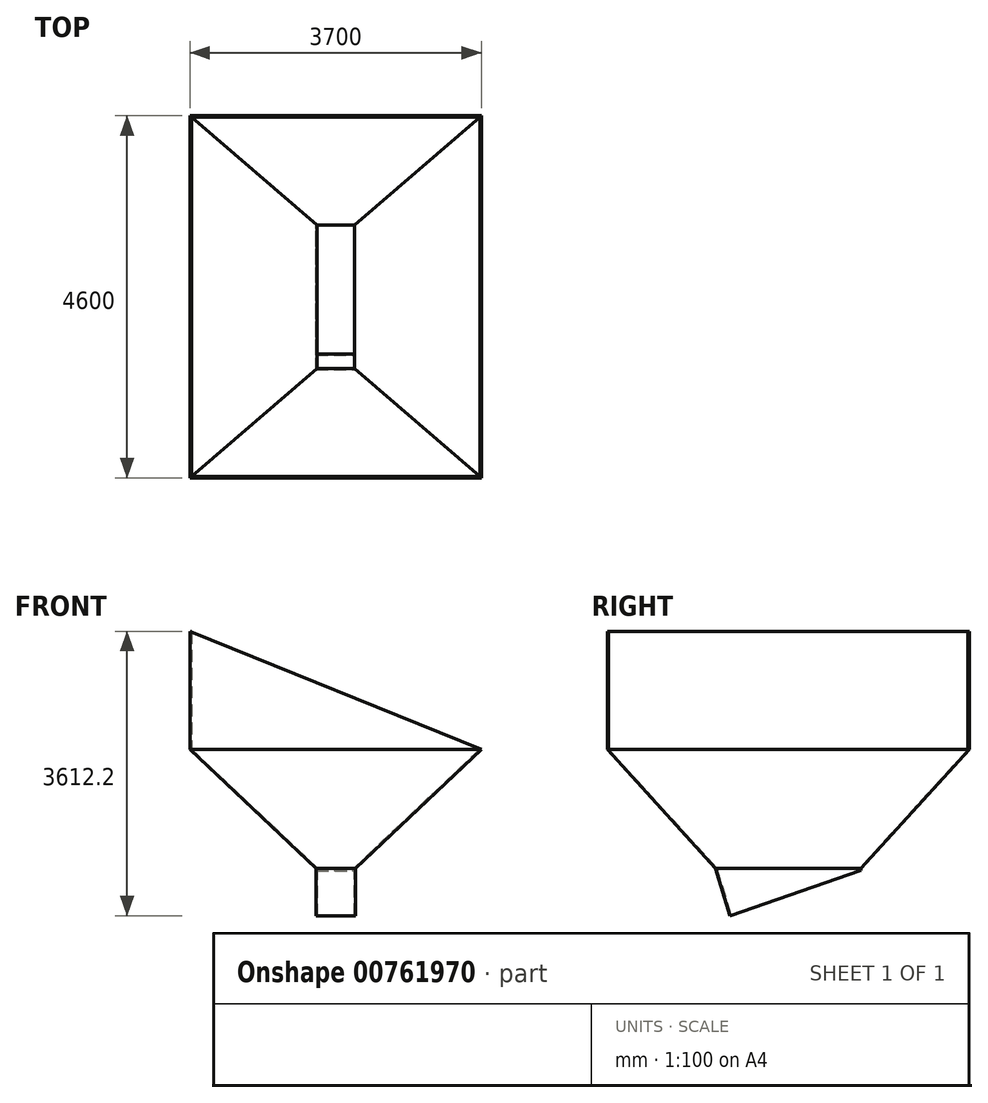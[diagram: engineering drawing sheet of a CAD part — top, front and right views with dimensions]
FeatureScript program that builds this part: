
annotation { "Feature Type Name" : "Feature", "Feature Type Description" : "" }
export const myFeature = defineFeature(function(context is Context, id is Id, definition is map)
    precondition{}
    {
        {
            var Q0;
            Q0=qCreatedBy(makeId("Top.planeOp"),FACE);
            var sketch = newSketch(context, id + "F0", { "sketchPlane" : qUnion([Q0])});
            skLineSegment(sketch, "E0.bottom", {"start": v(-1850, -2300) * mm, "end": v(1850, -2300) * mm});
            skLineSegment(sketch, "E0.top", {"start": v(-1850, 2300) * mm, "end": v(1850, 2300) * mm});
            skLineSegment(sketch, "E0.left", {"start": v(-1850, -2300) * mm, "end": v(-1850, 2300) * mm});
            skLineSegment(sketch, "E0.right", {"start": v(1850, -2300) * mm, "end": v(1850, 2300) * mm});
            skLineSegment(sketch, "E1", {"start": v(0, 2300) * mm, "end": v(0, -2300) * mm, "construction": true});
            skPoint(sketch, "E2", {"position": v(0, 0) * mm});
            skSolve(sketch);
        }
        {
            var Q0;
            Q0=makeQuery(id+"F0.imprint","IMPRINT",FACE,{"disambiguationData":[TD([[makeQuery(id+"F0.imprint","IMPRINT",EDGE,{"derivedFrom":sQuery(id+"F0.wireOp",EDGE,"E0.bottom")}),1.0]])]});
            cPlane(context, id + "F1", {"entities" : qUnion([Q0]), "cplaneType" : CPlaneType.OFFSET, "offset" : 1510 * mm, "oppositeDirection" : true, "width" : 150 * mm, "height" : 150 * mm});
        }
        {
            var Q0;
            Q0=qCreatedBy(id+"F1.planeOp",FACE);
            var sketch = newSketch(context, id + "F2", { "sketchPlane" : qUnion([Q0])});
            skLineSegment(sketch, "E3.0", {"start": v(0, 2300) * mm, "end": v(0, -2300) * mm, "construction": true});
            skPoint(sketch, "E4", {"position": v(0, 0) * mm});
            skLineSegment(sketch, "E5.bottom", {"start": v(-250, -925) * mm, "end": v(250, -925) * mm});
            skLineSegment(sketch, "E5.top", {"start": v(-250, 925) * mm, "end": v(250, 925) * mm});
            skLineSegment(sketch, "E5.left", {"start": v(-250, -925) * mm, "end": v(-250, 925) * mm});
            skLineSegment(sketch, "E5.right", {"start": v(250, -925) * mm, "end": v(250, 925) * mm});
            skLineSegment(sketch, "E6", {"start": v(-250, 925) * mm, "end": v(250, -925) * mm, "construction": true});
            skSolve(sketch);
        }
        {
            var Q0;
            Q0=makeQuery(id+"F0.imprint","IMPRINT",FACE,{"disambiguationData":[TD([[makeQuery(id+"F0.imprint","IMPRINT",EDGE,{"derivedFrom":sQuery(id+"F0.wireOp",EDGE,"E0.bottom")}),1.0]])]});
            var Q1;
            Q1=makeQuery(id+"F2.imprint","IMPRINT",FACE,{"disambiguationData":[TD([[makeQuery(id+"F2.imprint","IMPRINT",EDGE,{"derivedFrom":sQuery(id+"F2.wireOp",EDGE,"E5.bottom")}),1.0]])]});
            loft(context, id + "F3", {"sheetProfilesArray" : [{ "sheetProfileEntities" : qUnion([Q0]) }, { "sheetProfileEntities" : qUnion([Q1]) }]});
        }
        {
            var Q0;
            Q0=qCreatedBy(makeId("Right.planeOp"),FACE);
            var sketch = newSketch(context, id + "F4", { "sketchPlane" : qUnion([Q0])});
            skLineSegment(sketch, "E7.0", {"start": v(-2300, 0) * mm, "end": v(-925, -1510) * mm});
            skLineSegment(sketch, "E8", {"start": v(-925, -1510) * mm, "end": v(-739.92, -2112.2) * mm});
            skLineSegment(sketch, "E9", {"start": v(857.72, -2112.2) * mm, "end": v(-2628.46, -2112.2) * mm, "construction": true});
            skLineSegment(sketch, "E10.0", {"start": v(2300, 0) * mm, "end": v(925, -1510) * mm});
            skLineSegment(sketch, "E11", {"start": v(-739.92, -2112.2) * mm, "end": v(925, -1538.92) * mm});
            skLineSegment(sketch, "E12", {"start": v(925, -1538.92) * mm, "end": v(925, -1510) * mm});
            skLineSegment(sketch, "E13", {"start": v(925, -1510) * mm, "end": v(-925, -1510) * mm});
            skSolve(sketch);
        }
        {
            var Q0;
            Q0=makeQuery(id+"F4.imprint","IMPRINT",FACE,{"disambiguationData":[TD([[makeQuery(id+"F4.imprint","IMPRINT",EDGE,{"derivedFrom":sQuery(id+"F4.wireOp",EDGE,"E8")}),1.0]])]});
            extrude(context, id + "F5", {"entities" : qUnion([Q0]), "operationType" : NewBodyOperationType.ADD, "endBound" : BoundingType.SYMMETRIC, "oppositeDirection" : true, "depth" : 500 * mm, "offsetDistance" : 25 * mm});
        }
        {
            var Q0;
            Q0=makeQuery(id+"F3.opLoft","CAP_FACE",FACE,{"disambiguationData":[OSD([makeQuery(id+"F0.imprint","IMPRINT",FACE,{"disambiguationData":[TD([[makeQuery(id+"F0.imprint","IMPRINT",EDGE,{"derivedFrom":sQuery(id+"F0.wireOp",EDGE,"E0.bottom")}),1.0]])]})])],"isStart":true});
            var Q1;
            Q1=makeQuery(id+"F5.opExtrude","SWEPT_FACE",FACE,{"disambiguationData":[OSD([sQuery(id+"F4.wireOp",EDGE,"E11")])]});
            shell(context, id + "F6", {"entities" : qUnion([Q0, Q1]), "thickness" : 12.7 * mm});
        }
        {
            var Q0;
            Q0=makeQuery(id+"F3.opLoft","MID_CAP_EDGE",EDGE,{"disambiguationData":[OSD([sQuery(id+"F0.wireOp",EDGE,"E0.bottom"),sQuery(id+"F0.wireOp",EDGE,"E0.left"),sQuery(id+"F0.wireOp",EDGE,"E0.right")])],"capPos":0.0});
            cPlane(context, id + "F7", {"entities" : qUnion([Q0]), "cplaneType" : CPlaneType.LINE_ANGLE, "offset" : 25 * mm, "angle" : 0 * degree, "width" : 150 * mm, "height" : 150 * mm});
        }
        {
            var Q0;
            Q0=qCreatedBy(id+"F7.planeOp",FACE);
            var sketch = newSketch(context, id + "F8", { "sketchPlane" : qUnion([Q0])});
            skLineSegment(sketch, "E14.0", {"start": v(-1850, 0) * mm, "end": v(1850, 0) * mm});
            skLineSegment(sketch, "E15", {"start": v(1850, 0) * mm, "end": v(1850, 1500) * mm});
            skLineSegment(sketch, "E16", {"start": v(1850, 1500) * mm, "end": v(-1850, 0) * mm});
            skSolve(sketch);
        }
        {
            var Q0;
            Q0=makeQuery(id+"F8.imprint","IMPRINT",FACE,{"disambiguationData":[TD([[makeQuery(id+"F8.imprint","IMPRINT",EDGE,{"derivedFrom":sQuery(id+"F8.wireOp",EDGE,"E14.0")}),1.0]])]});
            extrude(context, id + "F9", {"entities" : qUnion([Q0]), "operationType" : NewBodyOperationType.ADD, "depth" : 6 * mm, "offsetDistance" : 25 * mm});
        }
        {
            var Q0;
            Q0=makeQuery(id+"F3.opLoft","MID_CAP_EDGE",EDGE,{"disambiguationData":[OSD([sQuery(id+"F0.wireOp",EDGE,"E0.top"),sQuery(id+"F0.wireOp",EDGE,"E0.left"),sQuery(id+"F0.wireOp",EDGE,"E0.right")])],"capPos":0.0});
            cPlane(context, id + "F10", {"entities" : qUnion([Q0]), "cplaneType" : CPlaneType.LINE_ANGLE, "offset" : 25 * mm, "angle" : 0 * degree, "width" : 150 * mm, "height" : 150 * mm});
        }
        {
            var Q0;
            Q0=qCreatedBy(id+"F10.planeOp",FACE);
            var sketch = newSketch(context, id + "F11", { "sketchPlane" : qUnion([Q0])});
            skLineSegment(sketch, "E17.0.0", {"start": v(1850, 0) * mm, "end": v(1850, 1500) * mm});
            skLineSegment(sketch, "E17.0.1", {"start": v(1850, 1500) * mm, "end": v(-1850, 0) * mm});
            skLineSegment(sketch, "E17.0.2", {"start": v(-1850, 0) * mm, "end": v(1850, 0) * mm});
            skSolve(sketch);
        }
        {
            var Q0;
            Q0=makeQuery(id+"F11.imprint","IMPRINT",FACE,{"disambiguationData":[TD([[makeQuery(id+"F11.imprint","IMPRINT",EDGE,{"derivedFrom":sQuery(id+"F11.wireOp",EDGE,"E17.0.0")}),1.0]])]});
            extrude(context, id + "F12", {"entities" : qUnion([Q0]), "operationType" : NewBodyOperationType.ADD, "oppositeDirection" : true, "depth" : 12.7 * mm, "offsetDistance" : 25 * mm});
        }
        {
            var Q0;
            Q0=makeQuery(id+"F12.opExtrude","CAP_FACE",FACE,{"disambiguationData":[OSD([sQuery(id+"F11.wireOp",EDGE,"E17.0.0"),sQuery(id+"F11.wireOp",EDGE,"E17.0.1"),sQuery(id+"F11.wireOp",EDGE,"E17.0.2")])],"isStart":false});
            var sketch = newSketch(context, id + "F13", { "sketchPlane" : qUnion([Q0])});
            skLineSegment(sketch, "E18.0", {"start": v(-1850, 0) * mm, "end": v(-1850, 1500) * mm});
            skLineSegment(sketch, "E19", {"start": v(-1850, 0) * mm, "end": v(-1841.26, 0) * mm});
            skLineSegment(sketch, "E20", {"start": v(-1841.26, 0) * mm, "end": v(-1841.26, 1496.46) * mm});
            skSolve(sketch);
        }
        {
            var Q0;
            {var subQ0=sQuery(id+"F13.wireOp",EDGE,"E18.0");Q0=makeQuery(id+"F13.imprint","IMPRINT",FACE,{"disambiguationData":[TD([[makeQuery(id+"F13.imprint","IMPRINT",EDGE,{"derivedFrom":subQ0}),-1.0]])]});}
            var Q1;
            Q1=makeQuery(id+"F3.opLoft","SWEPT_BODY",BODY,{"disambiguationData":[OSD([makeQuery(id+"F0.imprint","IMPRINT",FACE,{"disambiguationData":[TD([[makeQuery(id+"F0.imprint","IMPRINT",EDGE,{"derivedFrom":sQuery(id+"F0.wireOp",EDGE,"E0.bottom")}),1.0]])]}),makeQuery(id+"F2.imprint","IMPRINT",FACE,{"disambiguationData":[TD([[makeQuery(id+"F2.imprint","IMPRINT",EDGE,{"derivedFrom":sQuery(id+"F2.wireOp",EDGE,"E5.bottom")}),1.0]])]})])]});
            extrude(context, id + "F14", {"entities" : qUnion([Q0]), "operationType" : NewBodyOperationType.ADD, "endBound" : BoundingType.UP_TO_BODY, "depth" : 25 * mm, "endBoundEntityBody" : qUnion([Q1]), "offsetDistance" : 25 * mm});
        }
        {
            var Q0;
            Q0=makeQuery(id+"F9.opExtrude","CAP_FACE",FACE,{"disambiguationData":[OSD([sQuery(id+"F8.wireOp",EDGE,"E14.0"),sQuery(id+"F8.wireOp",EDGE,"E15"),sQuery(id+"F8.wireOp",EDGE,"E16")])],"isStart":false});
            var sketch = newSketch(context, id + "F15", { "sketchPlane" : qUnion([Q0])});
            skLineSegment(sketch, "E21.0", {"start": v(1841.26, 1496.46) * mm, "end": v(-1850, 0) * mm});
            skLineSegment(sketch, "E22.0", {"start": v(1841.26, 1496.46) * mm, "end": v(1841.26, 0) * mm});
            skLineSegment(sketch, "E23.0", {"start": v(-1850, 0) * mm, "end": v(1841.26, 0) * mm});
            skSolve(sketch);
        }
        {
            var Q0;
            Q0=makeQuery(id+"F15.imprint","IMPRINT",FACE,{"disambiguationData":[TD([[makeQuery(id+"F15.imprint","IMPRINT",EDGE,{"derivedFrom":sQuery(id+"F15.wireOp",EDGE,"E21.0")}),1.0]])]});
            var Q1;
            Q1=makeQuery(id+"F6.opShell","OFFSET_VERTEX",VERTEX,{"disambiguationData":[OSD([sQuery(id+"F0.wireOp",EDGE,"E0.bottom"),sQuery(id+"F0.wireOp",EDGE,"E0.left")])]});
            extrude(context, id + "F16", {"entities" : qUnion([Q0]), "operationType" : NewBodyOperationType.ADD, "endBound" : BoundingType.UP_TO_VERTEX, "depth" : 25 * mm, "endBoundEntityVertex" : qUnion([Q1]), "offsetDistance" : 25 * mm});
        }
        {
            var Q0;
            Q0=makeQuery(id+"F12.opExtrude","CAP_FACE",FACE,{"disambiguationData":[OSD([sQuery(id+"F11.wireOp",EDGE,"E17.0.0"),sQuery(id+"F11.wireOp",EDGE,"E17.0.1"),sQuery(id+"F11.wireOp",EDGE,"E17.0.2")])],"isStart":false});
            var sketch = newSketch(context, id + "F17", { "sketchPlane" : qUnion([Q0])});
            skLineSegment(sketch, "E24.0", {"start": v(-1841.26, 1496.46) * mm, "end": v(1850, 0) * mm});
            skLineSegment(sketch, "E25.0", {"start": v(1850, 0) * mm, "end": v(-1841.26, 0) * mm});
            skLineSegment(sketch, "E26.0", {"start": v(-1841.26, 0) * mm, "end": v(-1841.26, 1496.46) * mm});
            skSolve(sketch);
        }
        {
            var Q0;
            Q0=makeQuery(id+"F17.imprint","IMPRINT",FACE,{"disambiguationData":[TD([[makeQuery(id+"F17.imprint","IMPRINT",EDGE,{"derivedFrom":sQuery(id+"F17.wireOp",EDGE,"E24.0")}),-1.0]])]});
            var Q1;
            Q1=makeQuery(id+"F6.opShell","OFFSET_VERTEX",VERTEX,{"disambiguationData":[OSD([sQuery(id+"F0.wireOp",EDGE,"E0.top"),sQuery(id+"F0.wireOp",EDGE,"E0.left")])]});
            extrude(context, id + "F18", {"entities" : qUnion([Q0]), "operationType" : NewBodyOperationType.ADD, "endBound" : BoundingType.UP_TO_VERTEX, "depth" : 25 * mm, "endBoundEntityVertex" : qUnion([Q1]), "offsetDistance" : 25 * mm});
        }
        {
            var Q0;
            Q0=makeQuery(id+"F14.opExtrude","SWEPT_FACE",FACE,{"disambiguationData":[OSD([sQuery(id+"F13.wireOp",EDGE,"E20")])]});
            var sketch = newSketch(context, id + "F19", { "sketchPlane" : qUnion([Q0])});
            skLineSegment(sketch, "E27.0", {"start": v(-2282.82, 1496.46) * mm, "end": v(2282.82, 1496.46) * mm});
            skLineSegment(sketch, "E28.0", {"start": v(-2282.82, 1496.46) * mm, "end": v(-2282.82, 0) * mm});
            skLineSegment(sketch, "E29.0", {"start": v(-2282.82, 0) * mm, "end": v(2282.82, 0) * mm});
            skLineSegment(sketch, "E30.0", {"start": v(2282.82, 0) * mm, "end": v(2282.82, 1496.46) * mm});
            skSolve(sketch);
        }
        {
            var Q0;
            Q0=makeQuery(id+"F19.imprint","IMPRINT",FACE,{"disambiguationData":[TD([[makeQuery(id+"F19.imprint","IMPRINT",EDGE,{"derivedFrom":sQuery(id+"F19.wireOp",EDGE,"E27.0")}),-1.0]])]});
            var Q1;
            Q1=makeQuery(id+"F6.opShell","OFFSET_VERTEX",VERTEX,{"disambiguationData":[OSD([sQuery(id+"F0.wireOp",EDGE,"E0.top"),sQuery(id+"F0.wireOp",EDGE,"E0.left")])]});
            extrude(context, id + "F20", {"entities" : qUnion([Q0]), "operationType" : NewBodyOperationType.ADD, "endBound" : BoundingType.UP_TO_VERTEX, "depth" : 25 * mm, "endBoundEntityVertex" : qUnion([Q1]), "offsetDistance" : 25 * mm});
        }
    });
